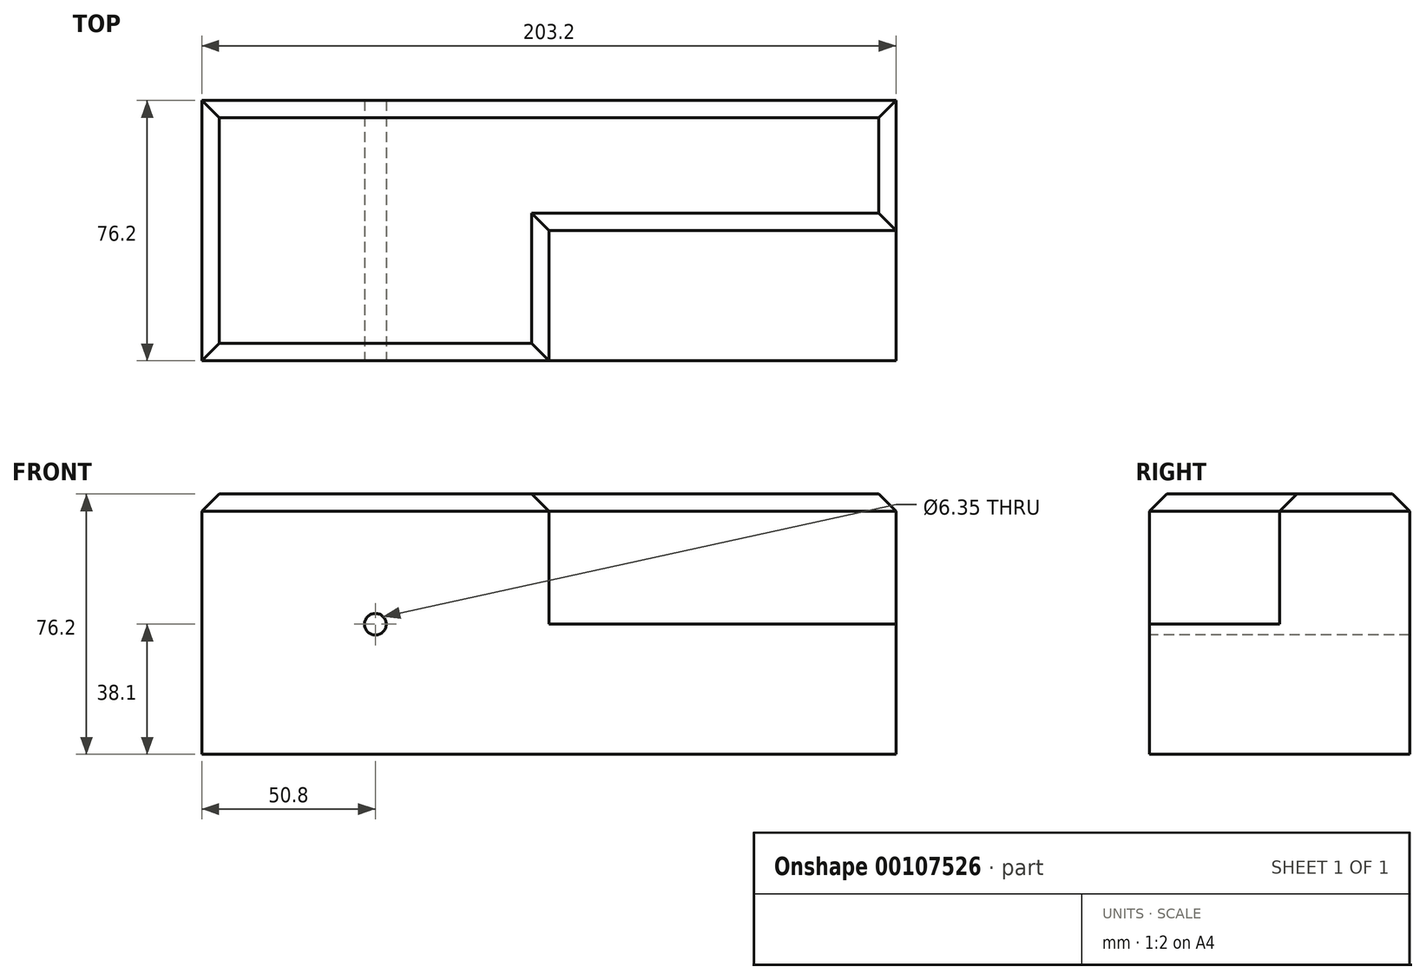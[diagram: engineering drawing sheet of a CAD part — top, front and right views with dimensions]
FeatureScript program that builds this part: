
annotation { "Feature Type Name" : "Feature", "Feature Type Description" : "" }
export const myFeature = defineFeature(function(context is Context, id is Id, definition is map)
    precondition{}
    {
        {
            var Q0;
            Q0=qCreatedBy(makeId("Front.planeOp"),FACE);
            var sketch = newSketch(context, id + "F0", { "sketchPlane" : qUnion([Q0])});
            skLineSegment(sketch, "E0", {"start": v(0, 0) * mm, "end": v(0, 76.2) * mm});
            skLineSegment(sketch, "E1", {"start": v(0, 76.2) * mm, "end": v(203.2, 76.2) * mm});
            skLineSegment(sketch, "E2", {"start": v(203.2, 76.2) * mm, "end": v(203.2, 0) * mm});
            skLineSegment(sketch, "E3", {"start": v(203.2, 0) * mm, "end": v(0, 0) * mm});
            skSolve(sketch);
        }
        {
            var Q0;
            Q0=makeQuery(id+"F0.imprint","IMPRINT",FACE,{"disambiguationData":[TD([[makeQuery(id+"F0.imprint","IMPRINT",EDGE,{"derivedFrom":sQuery(id+"F0.wireOp",EDGE,"E0")}),-1.0]])]});
            extrude(context, id + "F1", {"entities" : qUnion([Q0]), "depth" : 76.2 * mm});
        }
        {
            var Q0;
            Q0=makeQuery(id+"F1.opExtrude","SWEPT_FACE",FACE,{"disambiguationData":[OSD([sQuery(id+"F0.wireOp",EDGE,"E1")])]});
            var sketch = newSketch(context, id + "F2", { "sketchPlane" : qUnion([Q0])});
            skLineSegment(sketch, "E4.bottom", {"start": v(203.2, -76.2) * mm, "end": v(101.6, -76.2) * mm});
            skLineSegment(sketch, "E4.top", {"start": v(203.2, -38.1) * mm, "end": v(101.6, -38.1) * mm});
            skLineSegment(sketch, "E4.left", {"start": v(203.2, -76.2) * mm, "end": v(203.2, -38.1) * mm});
            skLineSegment(sketch, "E4.right", {"start": v(101.6, -76.2) * mm, "end": v(101.6, -38.1) * mm});
            skSolve(sketch);
        }
        {
            var Q0;
            Q0=makeQuery(id+"F2.imprint","IMPRINT",FACE,{"disambiguationData":[TD([[makeQuery(id+"F2.imprint","IMPRINT",EDGE,{"derivedFrom":sQuery(id+"F2.wireOp",EDGE,"E4.bottom")}),1.0]])]});
            extrude(context, id + "F3", {"entities" : qUnion([Q0]), "operationType" : NewBodyOperationType.REMOVE, "oppositeDirection" : true, "depth" : 38.1 * mm});
        }
        {
            var Q0;
            Q0=makeQuery(id+"F1.opExtrude","CAP_EDGE",EDGE,{"disambiguationData":[OSD([sQuery(id+"F0.wireOp",EDGE,"E1")])],"isStart":false});
            var Q1;
            Q1=makeQuery(id+"F1.opExtrude","SWEPT_FACE",FACE,{"disambiguationData":[OSD([sQuery(id+"F0.wireOp",EDGE,"E1")])]});
            chamfer(context, id + "F4", {"entities" : qUnion([Q0, Q1]), "width" : 5.08 * mm, "tangentPropagation" : true});
        }
        {
            var Q0;
            Q0=makeQuery(id+"F1.opExtrude","CAP_FACE",FACE,{"disambiguationData":[OSD([sQuery(id+"F0.wireOp",EDGE,"E0"),sQuery(id+"F0.wireOp",EDGE,"E1"),sQuery(id+"F0.wireOp",EDGE,"E2"),sQuery(id+"F0.wireOp",EDGE,"E3")])],"isStart":false});
            var sketch = newSketch(context, id + "F5", { "sketchPlane" : qUnion([Q0])});
            skLineSegment(sketch, "E5", {"start": v(0, 0) * mm, "end": v(50.8, 0) * mm});
            skLineSegment(sketch, "E6", {"start": v(50.8, 0) * mm, "end": v(50.8, 38.1) * mm});
            skSolve(sketch);
        }
        {
            var Q0;
            Q0=sQuery(id+"F5.wireOp",VERTEX,"E6.end");
            var Q1;
            Q1=makeQuery(id+"F1.opExtrude","SWEPT_BODY",BODY,{"disambiguationData":[OSD([sQuery(id+"F0.wireOp",EDGE,"E0"),sQuery(id+"F0.wireOp",EDGE,"E1"),sQuery(id+"F0.wireOp",EDGE,"E2"),sQuery(id+"F0.wireOp",EDGE,"E3")])]});
            hole(context, id + "F6", {"style" : HoleStyle.SIMPLE, "endStyle" : HoleEndStyle.THROUGH, "holeDiameter" : 6.35 * mm, "locations" : qUnion([Q0]), "scope" : qUnion([Q1]), "isTappedThrough" : true});
        }
    });
